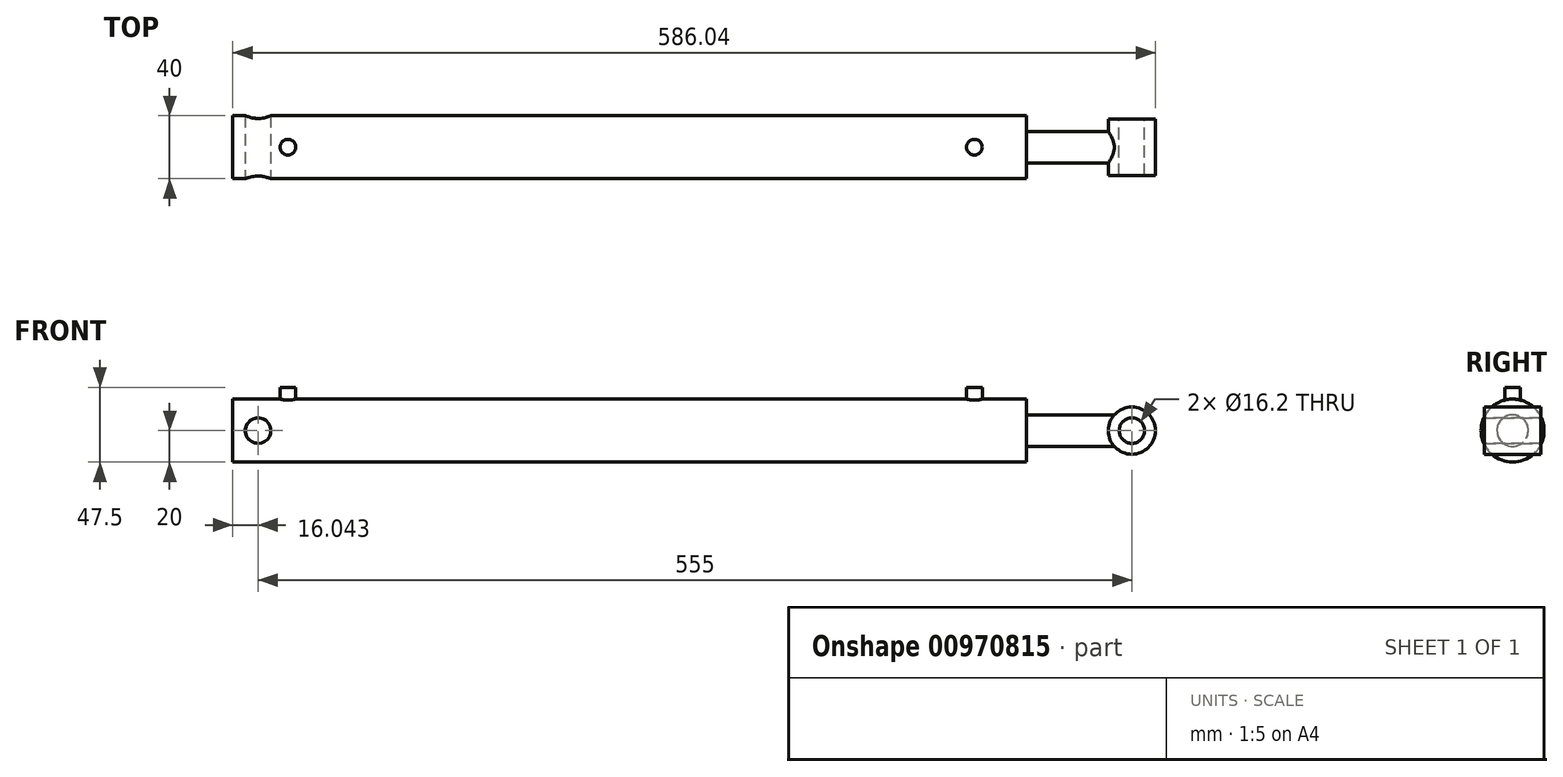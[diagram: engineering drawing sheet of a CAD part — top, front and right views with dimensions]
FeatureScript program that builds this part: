
annotation { "Feature Type Name" : "Feature", "Feature Type Description" : "" }
export const myFeature = defineFeature(function(context is Context, id is Id, definition is map)
    precondition{}
    {
        {
            var Q0;
            Q0=qCreatedBy(makeId("Front.planeOp"),FACE);
            var sketch = newSketch(context, id + "F0", { "sketchPlane" : qUnion([Q0])});
            skLineSegment(sketch, "E0", {"start": v(-302, 0) * mm, "end": v(143.84, 0) * mm, "construction": true});
            skLineSegment(sketch, "E1", {"start": v(0, 0) * mm, "end": v(0, 20) * mm});
            skLineSegment(sketch, "E2", {"start": v(0, 20) * mm, "end": v(504, 20) * mm});
            skLineSegment(sketch, "E3", {"start": v(504, 20) * mm, "end": v(504, 0) * mm});
            skLineSegment(sketch, "E4", {"start": v(504, 0) * mm, "end": v(0, 0) * mm});
            skPoint(sketch, "E5.orphan", {"position": v(460, 0) * mm});
            skSolve(sketch);
        }
        {
            var Q0;
            Q0=qSketchRegion(id+"F0",true);
            var Q1;
            Q1=sQuery(id+"F0.wireOp",EDGE,"E0");
            revolve(context, id + "F1", {"surfaceOperationType" : NewSurfaceOperationType.NEW, "entities" : qUnion([Q0]), "axis" : qUnion([Q1]), "revolveType" : RevolveType.FULL});
        }
        {
            var Q0;
            Q0=qCreatedBy(makeId("Front.planeOp"),FACE);
            cPlane(context, id + "F2", {"entities" : qUnion([Q0]), "cplaneType" : CPlaneType.OFFSET, "offset" : 17.5 * mm, "width" : 150 * mm, "height" : 150 * mm});
        }
        {
            var Q0;
            Q0=qCreatedBy(id+"F2.planeOp",FACE);
            var sketch = newSketch(context, id + "F3", { "sketchPlane" : qUnion([Q0])});
            skCircle(sketch, "E6", {"center": v(16.04, 0) * mm, "radius": 8.1 * mm});
            skSolve(sketch);
        }
        {
            var Q0;
            Q0=qSketchRegion(id+"F3",true);
            extrude(context, id + "F4", {"entities" : qUnion([Q0]), "operationType" : NewBodyOperationType.REMOVE, "endBound" : BoundingType.SYMMETRIC, "oppositeDirection" : true, "depth" : 100 * mm, "offsetDistance" : 25 * mm});
        }
        {
            var Q0;
            Q0=qCreatedBy(makeId("Front.planeOp"),FACE);
            var sketch = newSketch(context, id + "F5", { "sketchPlane" : qUnion([Q0])});
            skCircle(sketch, "E7", {"center": v(571.04, 0) * mm, "radius": 15 * mm});
            skCircle(sketch, "E8", {"center": v(571.04, 0) * mm, "radius": 8.1 * mm});
            skCircle(sketch, "E9", {"center": v(16.04, 0) * mm, "radius": 8.1 * mm, "construction": true});
            skSolve(sketch);
        }
        {
            var Q0;
            Q0=qSketchRegion(id+"F5",true);
            extrude(context, id + "F6", {"entities" : qUnion([Q0]), "operationType" : NewBodyOperationType.ADD, "endBound" : BoundingType.SYMMETRIC, "depth" : 36 * mm, "offsetDistance" : 25 * mm});
        }
        {
            var Q0;
            Q0=qCreatedBy(makeId("Top.planeOp"),FACE);
            cPlane(context, id + "F7", {"entities" : qUnion([Q0]), "cplaneType" : CPlaneType.OFFSET, "offset" : 17.5 * mm, "width" : 150 * mm, "height" : 150 * mm});
        }
        {
            var Q0;
            Q0=qCreatedBy(id+"F7.planeOp",FACE);
            var sketch = newSketch(context, id + "F8", { "sketchPlane" : qUnion([Q0])});
            skCircle(sketch, "E10", {"center": v(35, 0) * mm, "radius": 5 * mm});
            skCircle(sketch, "E11", {"center": v(471, 0) * mm, "radius": 5 * mm});
            skSolve(sketch);
        }
        {
            var Q0;
            Q0=qSketchRegion(id+"F8",true);
            extrude(context, id + "F9", {"entities" : qUnion([Q0]), "operationType" : NewBodyOperationType.ADD, "depth" : 10 * mm, "offsetDistance" : 25 * mm});
        }
        {
            var Q0;
            Q0=makeQuery(id+"F6.opExtrude","SWEPT_FACE",FACE,{"disambiguationData":[OSD([sQuery(id+"F5.wireOp",EDGE,"E7")])]});
            cPlane(context, id + "F10", {"entities" : qUnion([Q0]), "cplaneType" : CPlaneType.LINE_ANGLE, "offset" : 25 * mm, "angle" : 90 * degree, "width" : 150 * mm, "height" : 150 * mm});
        }
        {
            var Q0;
            Q0=qCreatedBy(id+"F10.planeOp",FACE);
            cPlane(context, id + "F11", {"entities" : qUnion([Q0]), "cplaneType" : CPlaneType.OFFSET, "offset" : 10 * mm, "oppositeDirection" : true, "width" : 150 * mm, "height" : 150 * mm});
        }
        {
            var Q0;
            Q0=qCreatedBy(id+"F11.planeOp",FACE);
            var sketch = newSketch(context, id + "F12", { "sketchPlane" : qUnion([Q0])});
            skCircle(sketch, "E12", {"center": v(0, 0) * mm, "radius": 10 * mm});
            skSolve(sketch);
        }
        {
            var Q0;
            Q0=qSketchRegion(id+"F12",true);
            extrude(context, id + "F13", {"entities" : qUnion([Q0]), "operationType" : NewBodyOperationType.ADD, "oppositeDirection" : true, "depth" : 400 * mm, "offsetDistance" : 25 * mm});
        }
    });
